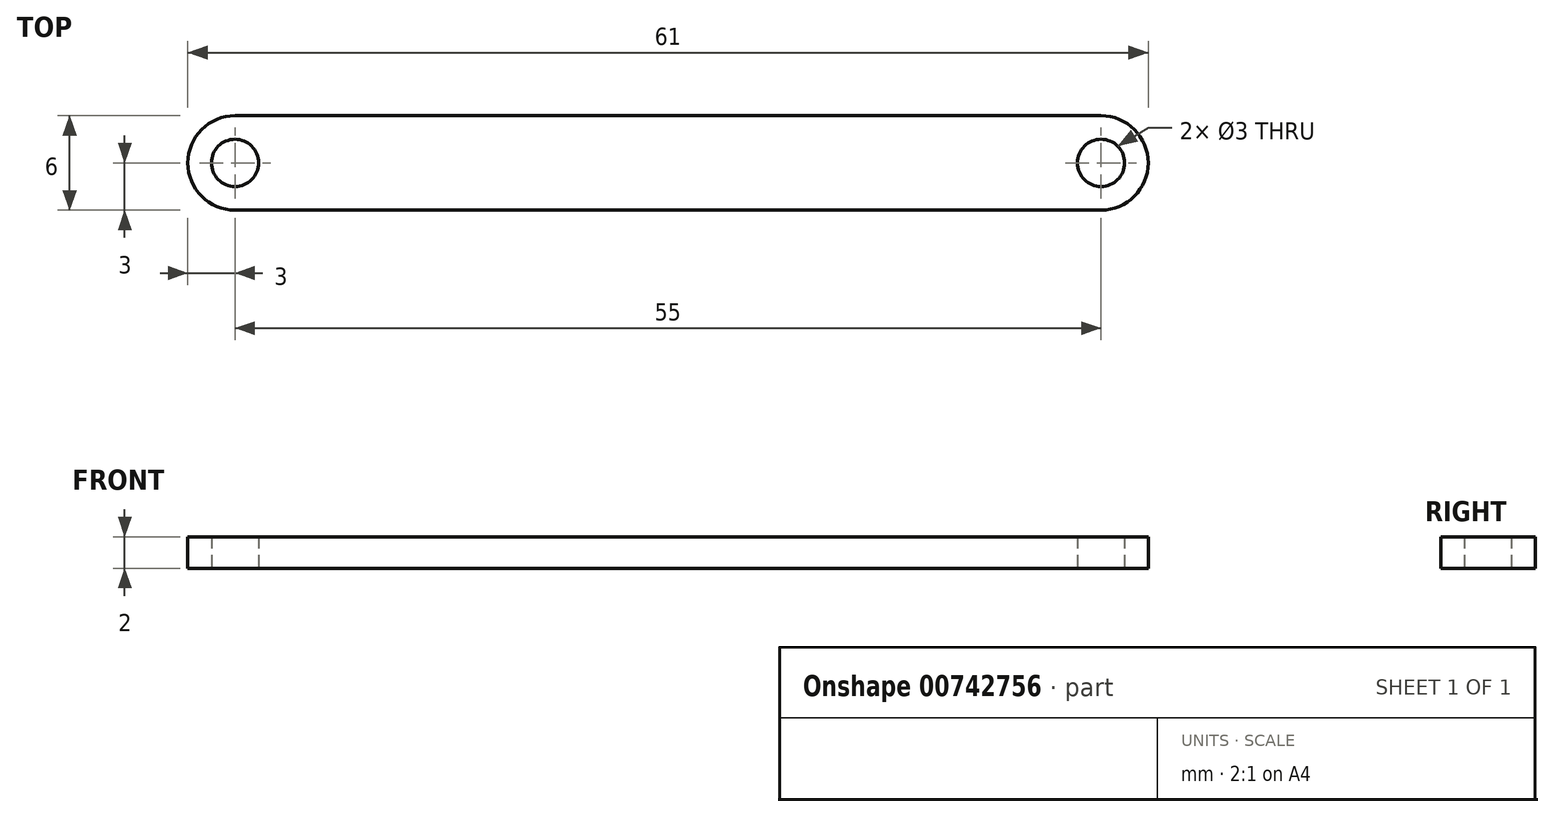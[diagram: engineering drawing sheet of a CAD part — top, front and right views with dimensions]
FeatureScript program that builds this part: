
annotation { "Feature Type Name" : "Feature", "Feature Type Description" : "" }
export const myFeature = defineFeature(function(context is Context, id is Id, definition is map)
    precondition{}
    {
        {
            var Q0;
            Q0=qCreatedBy(makeId("Top.planeOp"),FACE);
            var sketch = newSketch(context, id + "F0", { "sketchPlane" : qUnion([Q0])});
            skLineSegment(sketch, "E0.bottom", {"start": v(27.5, -3) * mm, "end": v(-27.5, -3) * mm});
            skLineSegment(sketch, "E0.top", {"start": v(27.5, 3) * mm, "end": v(-27.5, 3) * mm});
            skPoint(sketch, "E0.middle", {"position": v(0, 0) * mm});
            skArc(sketch, "E1", {"start": v(-27.5, 3) * mm, "mid": v(-30.5, 0) * mm, "end": v(-27.5, -3) * mm});
            skArc(sketch, "E2", {"start": v(27.5, -3) * mm, "mid": v(30.5, 0) * mm, "end": v(27.5, 3) * mm});
            skCircle(sketch, "E3", {"center": v(-27.5, 0) * mm, "radius": 1.5 * mm});
            skCircle(sketch, "E4", {"center": v(27.5, 0) * mm, "radius": 1.5 * mm});
            skSolve(sketch);
        }
        {
            var Q0;
            Q0 = qSketchRegion(id + "F0", true);
            extrude(context, id + "F1", {"entities" : qUnion([Q0]), "depth" : 2 * mm, "offsetDistance" : 25 * mm});
        }
    });
